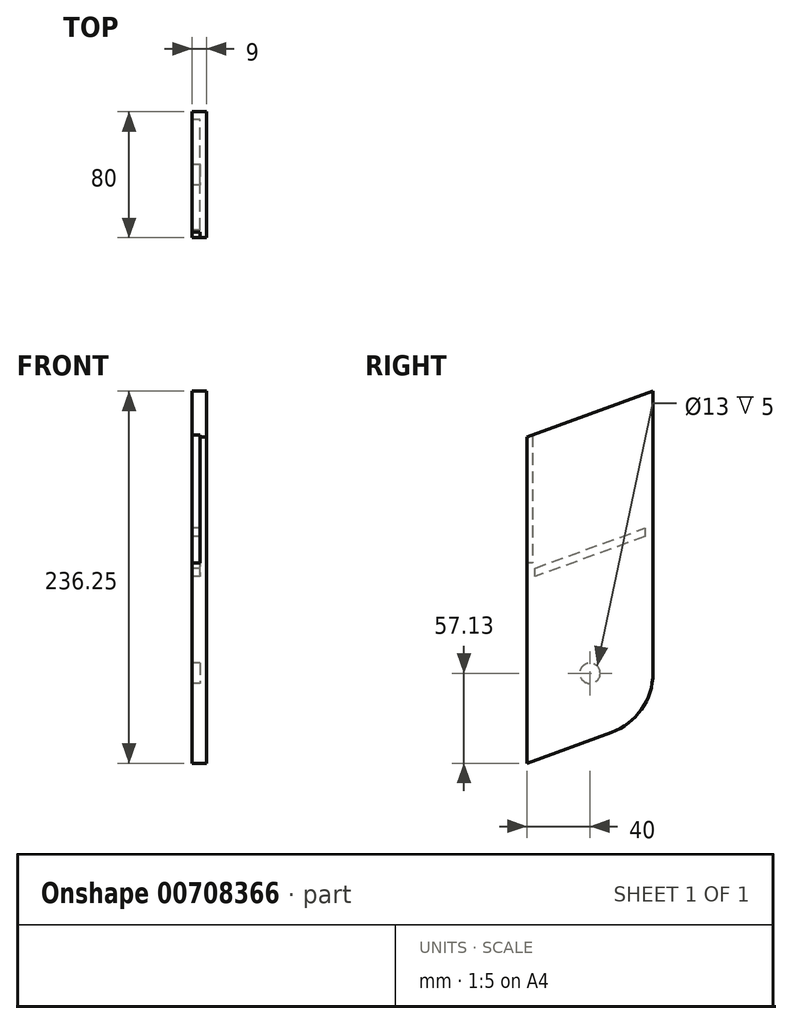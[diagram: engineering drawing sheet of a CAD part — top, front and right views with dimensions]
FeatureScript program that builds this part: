
annotation { "Feature Type Name" : "Feature", "Feature Type Description" : "" }
export const myFeature = defineFeature(function(context is Context, id is Id, definition is map)
    precondition{}
    {
        {
            var Q0;
            Q0=qCreatedBy(makeId("Right.planeOp"),FACE);
            var sketch = newSketch(context, id + "F0", { "sketchPlane" : qUnion([Q0])});
            skLineSegment(sketch, "E0", {"start": v(0, 0) * mm, "end": v(80, 29.12) * mm});
            skLineSegment(sketch, "E1", {"start": v(80, 29.12) * mm, "end": v(80, -150) * mm});
            skLineSegment(sketch, "E2", {"start": v(53.68, -187.59) * mm, "end": v(0, -207.13) * mm});
            skLineSegment(sketch, "E3", {"start": v(0, -207.13) * mm, "end": v(0, 0) * mm});
            skPoint(sketch, "E4.visualSharp", {"position": v(80, -178) * mm});
            skArc(sketch, "E4.filletArc", {"start": v(53.68, -187.59) * mm, "mid": v(72.77, -172.94) * mm, "end": v(80, -150) * mm});
            skSolve(sketch);
        }
        {
            var Q0;
            Q0=makeQuery(id+"F0.imprint","IMPRINT",FACE,{"disambiguationData":[TD([[makeQuery(id+"F0.imprint","IMPRINT",EDGE,{"derivedFrom":sQuery(id+"F0.wireOp",EDGE,"E0")}),-1.0]])]});
            extrude(context, id + "F1", {"entities" : qUnion([Q0]), "depth" : 9 * mm, "offsetDistance" : 25 * mm});
        }
        {
            var Q0;
            Q0=makeQuery(id+"F1.opExtrude","CAP_FACE",FACE,{"disambiguationData":[OSD([sQuery(id+"F0.wireOp",EDGE,"E0"),sQuery(id+"F0.wireOp",EDGE,"E1"),sQuery(id+"F0.wireOp",EDGE,"E2"),sQuery(id+"F0.wireOp",EDGE,"E3"),sQuery(id+"F0.wireOp",EDGE,"E4.filletArc")])],"isStart":true});
            var sketch = newSketch(context, id + "F2", { "sketchPlane" : qUnion([Q0])});
            skCircle(sketch, "E5", {"center": v(-40, -150) * mm, "radius": 6.5 * mm});
            skSolve(sketch);
        }
        {
            var Q0;
            Q0 = qSketchRegion(id + "F2", true);
            extrude(context, id + "F3", {"entities" : qUnion([Q0]), "operationType" : NewBodyOperationType.REMOVE, "oppositeDirection" : true, "depth" : 5 * mm, "offsetDistance" : 25 * mm});
        }
        {
            var Q0;
            Q0=makeQuery(id+"F1.opExtrude","CAP_FACE",FACE,{"disambiguationData":[OSD([sQuery(id+"F0.wireOp",EDGE,"E0"),sQuery(id+"F0.wireOp",EDGE,"E1"),sQuery(id+"F0.wireOp",EDGE,"E2"),sQuery(id+"F0.wireOp",EDGE,"E3"),sQuery(id+"F0.wireOp",EDGE,"E4.filletArc")])],"isStart":true});
            var sketch = newSketch(context, id + "F4", { "sketchPlane" : qUnion([Q0])});
            skLineSegment(sketch, "E6", {"start": v(-5, -83.31) * mm, "end": v(-75, -57.84) * mm});
            skLineSegment(sketch, "E7", {"start": v(-75, -57.84) * mm, "end": v(-75, -63.16) * mm});
            skLineSegment(sketch, "E8", {"start": v(-75, -63.16) * mm, "end": v(-5, -88.64) * mm});
            skLineSegment(sketch, "E9", {"start": v(-5, -88.64) * mm, "end": v(-5, -83.31) * mm});
            skSolve(sketch);
        }
        {
            var Q0;
            Q0 = qSketchRegion(id + "F4", true);
            extrude(context, id + "F5", {"entities" : qUnion([Q0]), "operationType" : NewBodyOperationType.REMOVE, "oppositeDirection" : true, "depth" : 5 * mm, "offsetDistance" : 25 * mm});
        }
        {
            var Q0;
            Q0=makeQuery(id+"F1.opExtrude","CAP_FACE",FACE,{"disambiguationData":[OSD([sQuery(id+"F0.wireOp",EDGE,"E0"),sQuery(id+"F0.wireOp",EDGE,"E1"),sQuery(id+"F0.wireOp",EDGE,"E2"),sQuery(id+"F0.wireOp",EDGE,"E3"),sQuery(id+"F0.wireOp",EDGE,"E4.filletArc")])],"isStart":true});
            var sketch = newSketch(context, id + "F6", { "sketchPlane" : qUnion([Q0])});
            skLineSegment(sketch, "E10", {"start": v(-3.5, 1.27) * mm, "end": v(-3.5, -80) * mm});
            skLineSegment(sketch, "E11", {"start": v(-3.5, -80) * mm, "end": v(0, -80) * mm});
            skLineSegment(sketch, "E12", {"start": v(-3.5, 1.27) * mm, "end": v(0, 0) * mm});
            skLineSegment(sketch, "E13", {"start": v(0, 0) * mm, "end": v(0, -80) * mm});
            skSolve(sketch);
        }
        {
            var Q0;
            Q0 = qSketchRegion(id + "F6", true);
            extrude(context, id + "F7", {"entities" : qUnion([Q0]), "operationType" : NewBodyOperationType.REMOVE, "oppositeDirection" : true, "depth" : 5 * mm, "offsetDistance" : 25 * mm});
        }
    });
